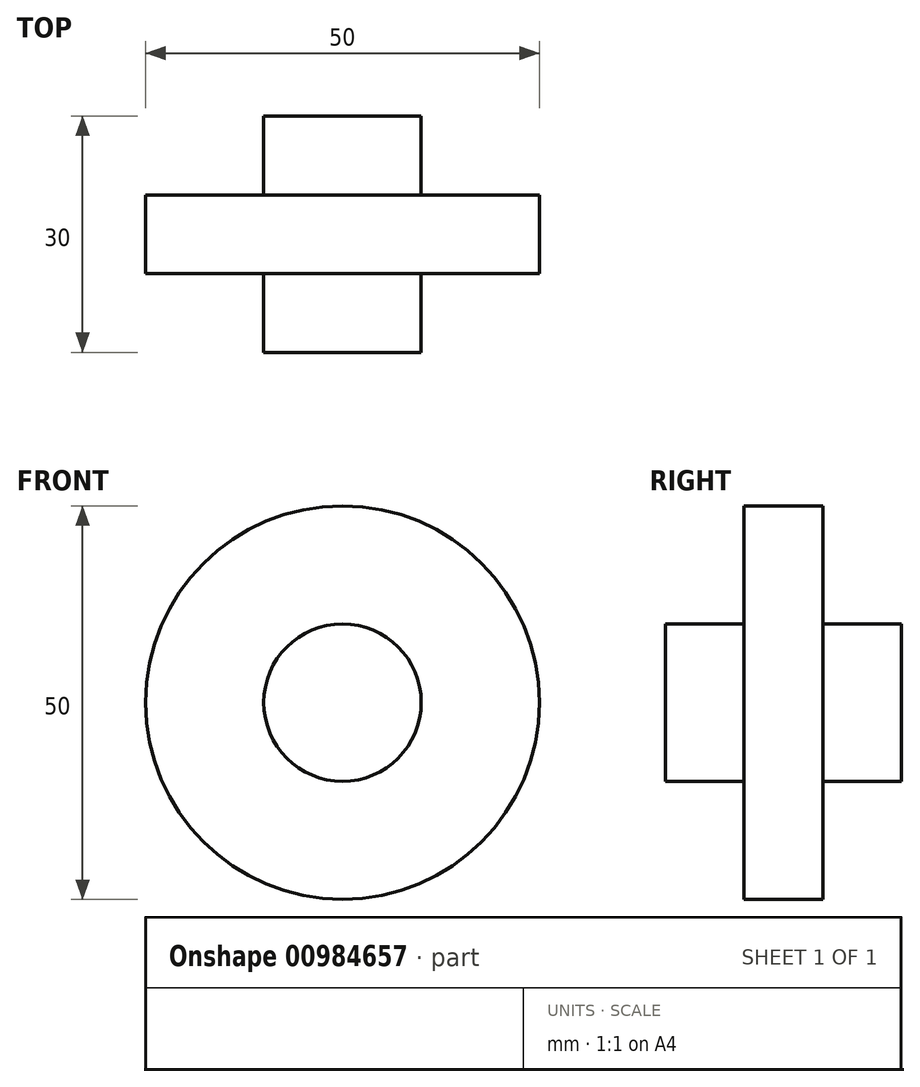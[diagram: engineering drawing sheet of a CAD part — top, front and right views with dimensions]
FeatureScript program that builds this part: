
annotation { "Feature Type Name" : "Feature", "Feature Type Description" : "" }
export const myFeature = defineFeature(function(context is Context, id is Id, definition is map)
    precondition{}
    {
        {
            var Q0;
            Q0=qCreatedBy(makeId("Front.planeOp"),FACE);
            var sketch = newSketch(context, id + "F0", { "sketchPlane" : qUnion([Q0])});
            skCircle(sketch, "E0", {"center": v(0, 0) * mm, "radius": 10 * mm});
            skCircle(sketch, "E1", {"center": v(0, 0) * mm, "radius": 25 * mm});
            skSolve(sketch);
        }
        {
            var Q0;
            Q0=makeQuery(id+"F0.imprint","IMPRINT",FACE,{"disambiguationData":[TD([[makeQuery(id+"F0.imprint","IMPRINT",EDGE,{"derivedFrom":sQuery(id+"F0.wireOp",EDGE,"E0")}),1.0]])]});
            extrude(context, id + "F1", {"entities" : qUnion([Q0]), "depth" : 15 * mm, "offsetDistance" : 25 * mm});
        }
        {
            var Q0;
            Q0=makeQuery(id+"F0.imprint","IMPRINT",FACE,{"disambiguationData":[TD([[makeQuery(id+"F0.imprint","IMPRINT",EDGE,{"derivedFrom":sQuery(id+"F0.wireOp",EDGE,"E0")}),1.0]])]});
            extrude(context, id + "F2", {"entities" : qUnion([Q0]), "operationType" : NewBodyOperationType.ADD, "oppositeDirection" : true, "depth" : 15 * mm, "offsetDistance" : 25 * mm});
        }
        {
            var Q0;
            Q0=makeQuery(id+"F0.imprint","IMPRINT",FACE,{"disambiguationData":[TD([[makeQuery(id+"F0.imprint","IMPRINT",EDGE,{"derivedFrom":sQuery(id+"F0.wireOp",EDGE,"E0")}),-1.0]])]});
            extrude(context, id + "F3", {"entities" : qUnion([Q0]), "operationType" : NewBodyOperationType.ADD, "depth" : 5 * mm, "offsetDistance" : 25 * mm});
        }
        {
            var Q0;
            Q0=makeQuery(id+"F0.imprint","IMPRINT",FACE,{"disambiguationData":[TD([[makeQuery(id+"F0.imprint","IMPRINT",EDGE,{"derivedFrom":sQuery(id+"F0.wireOp",EDGE,"E0")}),-1.0]])]});
            extrude(context, id + "F4", {"entities" : qUnion([Q0]), "operationType" : NewBodyOperationType.ADD, "oppositeDirection" : true, "depth" : 5 * mm, "offsetDistance" : 25 * mm});
        }
    });
